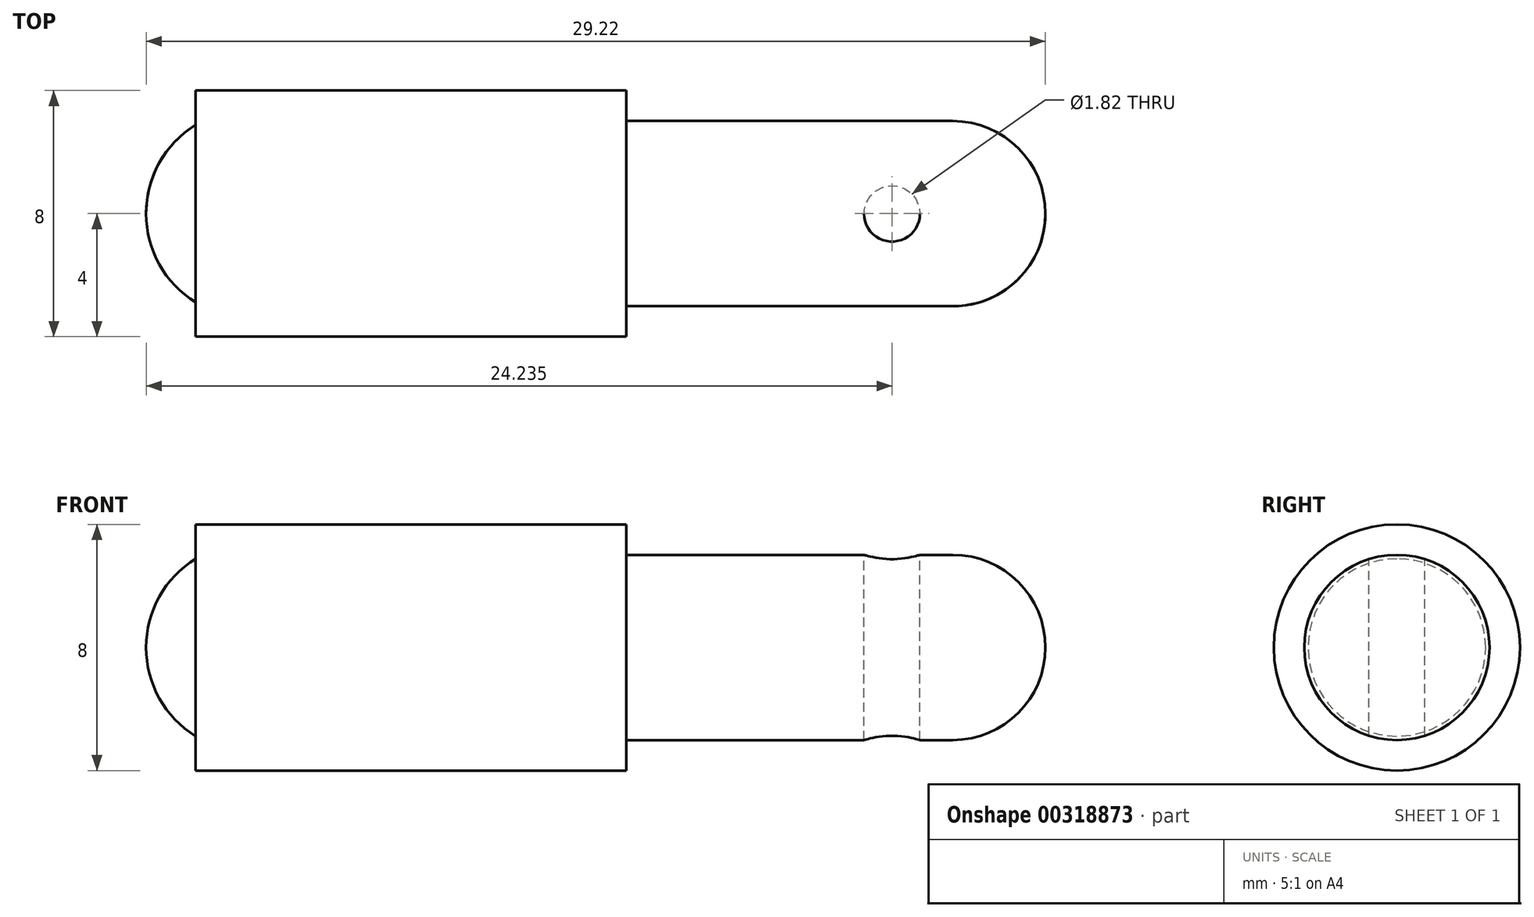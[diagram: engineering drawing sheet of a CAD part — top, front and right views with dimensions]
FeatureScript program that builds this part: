
annotation { "Feature Type Name" : "Feature", "Feature Type Description" : "" }
export const myFeature = defineFeature(function(context is Context, id is Id, definition is map)
    precondition{}
    {
        {
            var Q0;
            Q0=qCreatedBy(makeId("Top.planeOp"),FACE);
            var sketch = newSketch(context, id + "F0", { "sketchPlane" : qUnion([Q0])});
            skLineSegment(sketch, "E0", {"start": v(-16.87, 4) * mm, "end": v(-2.87, 4) * mm});
            skLineSegment(sketch, "E1", {"start": v(-2.87, 4) * mm, "end": v(-2.87, 0) * mm});
            skLineSegment(sketch, "E2", {"start": v(-2.87, 0) * mm, "end": v(-16.87, 0) * mm});
            skLineSegment(sketch, "E3", {"start": v(-16.87, 0) * mm, "end": v(-16.87, 4) * mm});
            skLineSegment(sketch, "E4", {"start": v(-2.87, 3) * mm, "end": v(7.74, 3.01) * mm});
            skLineSegment(sketch, "E5", {"start": v(7.74, 3.01) * mm, "end": v(7.74, 0) * mm});
            skLineSegment(sketch, "E6", {"start": v(7.74, 0) * mm, "end": v(-2.87, 0) * mm});
            skLineSegment(sketch, "E7", {"start": v(7.74, 0) * mm, "end": v(10.75, 0) * mm});
            skLineSegment(sketch, "E8", {"start": v(7.74, 0) * mm, "end": v(93.34, 0) * mm, "construction": true});
            skPoint(sketch, "E8.endSnap0", {"position": v(9.24, 0) * mm});
            skLineSegment(sketch, "E9", {"start": v(-16.87, 0) * mm, "end": v(-16.64, 0) * mm});
            skLineSegment(sketch, "E10", {"start": v(-18.47, 0) * mm, "end": v(-16.64, 0) * mm});
            skLineSegment(sketch, "E11", {"start": v(7.74, 3.01) * mm, "end": v(10.75, 3.01) * mm, "construction": true});
            skLineSegment(sketch, "E12", {"start": v(10.75, 3.01) * mm, "end": v(10.75, 0) * mm, "construction": true});
            skArc(sketch, "E13", {"start": v(10.75, 0) * mm, "mid": v(9.87, 2.13) * mm, "end": v(7.74, 3.01) * mm});
            skLineSegment(sketch, "E14", {"start": v(-16.64, 3) * mm, "end": v(-18.47, 3) * mm, "construction": true});
            skLineSegment(sketch, "E15", {"start": v(-18.47, 0) * mm, "end": v(-18.47, 3) * mm, "construction": true});
            skLineSegment(sketch, "E16", {"start": v(-16.87, 3) * mm, "end": v(-16.64, 3) * mm});
            skArc(sketch, "E17", {"start": v(-16.64, 3) * mm, "mid": v(-17.98, 1.76) * mm, "end": v(-18.47, 0) * mm});
            skSolve(sketch);
        }
        {
            var Q0;
            Q0=qCreatedBy(makeId("Top.planeOp"),FACE);
            var sketch = newSketch(context, id + "F1", { "sketchPlane" : qUnion([Q0])});
            skCircle(sketch, "E18", {"center": v(5.77, 0) * mm, "radius": 0.9 * mm});
            skSolve(sketch);
        }
        {
            var Q0;
            Q0 = qSketchRegion(id + "F0", true);
            var Q1;
            Q1=sQuery(id+"F0.wireOp",EDGE,"E8");
            revolve(context, id + "F2", {"entities" : qUnion([Q0]), "axis" : qUnion([Q1]), "revolveType" : RevolveType.FULL});
        }
        {
            var Q0;
            Q0 = qSketchRegion(id + "F1", true);
            extrude(context, id + "F3", {"entities" : qUnion([Q0]), "operationType" : NewBodyOperationType.REMOVE, "oppositeDirection" : true, "depth" : 25 * mm, "hasSecondDirection" : true, "secondDirectionOppositeDirection" : false, "secondDirectionDepth" : 25 * mm});
        }
    });
